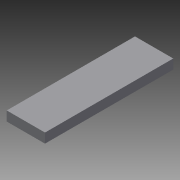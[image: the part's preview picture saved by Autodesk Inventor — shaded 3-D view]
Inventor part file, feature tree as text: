
AUTODESK INVENTOR PART (.ipt)
format: ipt  version: 2013 (Build 170138000, 138)  size: 66,048 bytes
history: native  units: in
note: dims shown in document units (in); Inventor stores cm internally (conversion verified against a paired STEP export)
features: extrude x1, sketch x1
ambient origin geometry x8: Origin, YZ Plane, XZ Plane, XY Plane, X Axis, Y Axis, Z Axis, Center Point
bodies: Solid1 (feature_tree)
feature tree (2):
  extrude  "Extrusion1"  Depth=3.35in
  sketch  "Sketch1"  dims[d0=1.0in d2=3.35in d3=0.25in d4=0.0in]
